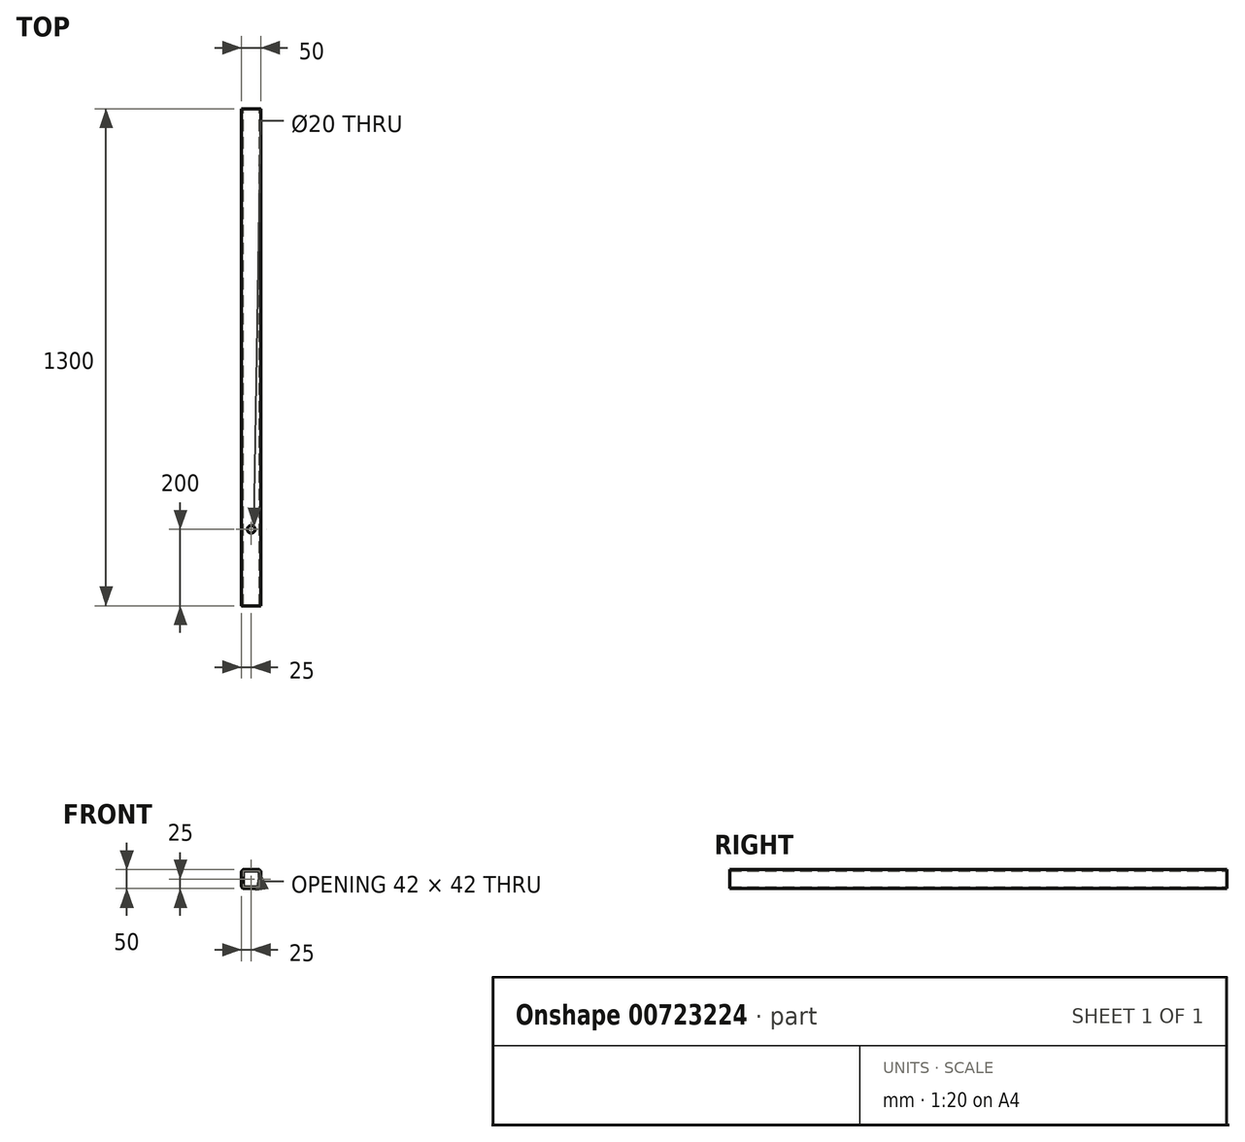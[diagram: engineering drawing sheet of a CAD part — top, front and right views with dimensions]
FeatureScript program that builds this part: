
annotation { "Feature Type Name" : "Feature", "Feature Type Description" : "" }
export const myFeature = defineFeature(function(context is Context, id is Id, definition is map)
    precondition{}
    {
        {
            var Q0;
            Q0=qCreatedBy(makeId("Front.planeOp"),FACE);
            var sketch = newSketch(context, id + "F0", { "sketchPlane" : qUnion([Q0])});
            skLineSegment(sketch, "E0.bottom", {"start": v(-19, 25) * mm, "end": v(19, 25) * mm});
            skLineSegment(sketch, "E0.top", {"start": v(-19, -25) * mm, "end": v(19, -25) * mm});
            skLineSegment(sketch, "E0.left", {"start": v(-25, 19) * mm, "end": v(-25, -19) * mm});
            skLineSegment(sketch, "E0.right", {"start": v(25, 19) * mm, "end": v(25, -19) * mm});
            skLineSegment(sketch, "E1.bottom", {"start": v(-19, 21) * mm, "end": v(19, 21) * mm});
            skLineSegment(sketch, "E1.top", {"start": v(-19, -21) * mm, "end": v(19, -21) * mm});
            skLineSegment(sketch, "E1.left", {"start": v(-21, 19) * mm, "end": v(-21, -19) * mm});
            skLineSegment(sketch, "E1.right", {"start": v(21, 19) * mm, "end": v(21, -19) * mm});
            skPoint(sketch, "E2.visualSharp", {"position": v(-21, 21) * mm});
            skArc(sketch, "E2.filletArc", {"start": v(-19, 21) * mm, "mid": v(-20.41, 20.41) * mm, "end": v(-21, 19) * mm});
            skPoint(sketch, "E3.visualSharp", {"position": v(21, 21) * mm});
            skArc(sketch, "E3.filletArc", {"start": v(21, 19) * mm, "mid": v(20.41, 20.41) * mm, "end": v(19, 21) * mm});
            skPoint(sketch, "E4.visualSharp", {"position": v(21, -21) * mm});
            skArc(sketch, "E4.filletArc", {"start": v(19, -21) * mm, "mid": v(20.41, -20.41) * mm, "end": v(21, -19) * mm});
            skPoint(sketch, "E5.visualSharp", {"position": v(-21, -21) * mm});
            skArc(sketch, "E5.filletArc", {"start": v(-21, -19) * mm, "mid": v(-20.41, -20.41) * mm, "end": v(-19, -21) * mm});
            skPoint(sketch, "E6.visualSharp", {"position": v(-25, 25) * mm});
            skArc(sketch, "E6.filletArc", {"start": v(-19, 25) * mm, "mid": v(-23.24, 23.24) * mm, "end": v(-25, 19) * mm});
            skPoint(sketch, "E7.visualSharp", {"position": v(25, 25) * mm});
            skArc(sketch, "E7.filletArc", {"start": v(25, 19) * mm, "mid": v(23.24, 23.24) * mm, "end": v(19, 25) * mm});
            skPoint(sketch, "E8.visualSharp", {"position": v(25, -25) * mm});
            skArc(sketch, "E8.filletArc", {"start": v(19, -25) * mm, "mid": v(23.24, -23.24) * mm, "end": v(25, -19) * mm});
            skPoint(sketch, "E9.visualSharp", {"position": v(-25, -25) * mm});
            skArc(sketch, "E9.filletArc", {"start": v(-25, -19) * mm, "mid": v(-23.24, -23.24) * mm, "end": v(-19, -25) * mm});
            skSolve(sketch);
        }
        {
            var Q0;
            Q0=makeQuery(id+"F0.imprint","IMPRINT",FACE,{"disambiguationData":[TD([[makeQuery(id+"F0.imprint","IMPRINT",EDGE,{"derivedFrom":sQuery(id+"F0.wireOp",EDGE,"E0.bottom")}),-1.0]])]});
            extrude(context, id + "F1", {"entities" : qUnion([Q0]), "endBound" : BoundingType.SYMMETRIC, "depth" : 1300 * mm, "offsetDistance" : 25 * mm});
        }
        {
            var Q0;
            Q0=makeQuery(id+"F1.opExtrude","SWEPT_FACE",FACE,{"disambiguationData":[OSD([sQuery(id+"F0.wireOp",EDGE,"E0.bottom")])]});
            var sketch = newSketch(context, id + "F2", { "sketchPlane" : qUnion([Q0])});
            skCircle(sketch, "E10", {"center": v(0, -450) * mm, "radius": 10 * mm});
            skSolve(sketch);
        }
        {
            var Q0;
            Q0 = qSketchRegion(id + "F2", true);
            extrude(context, id + "F3", {"entities" : qUnion([Q0]), "operationType" : NewBodyOperationType.REMOVE, "oppositeDirection" : true, "depth" : 25 * mm, "offsetDistance" : 25 * mm});
        }
    });
